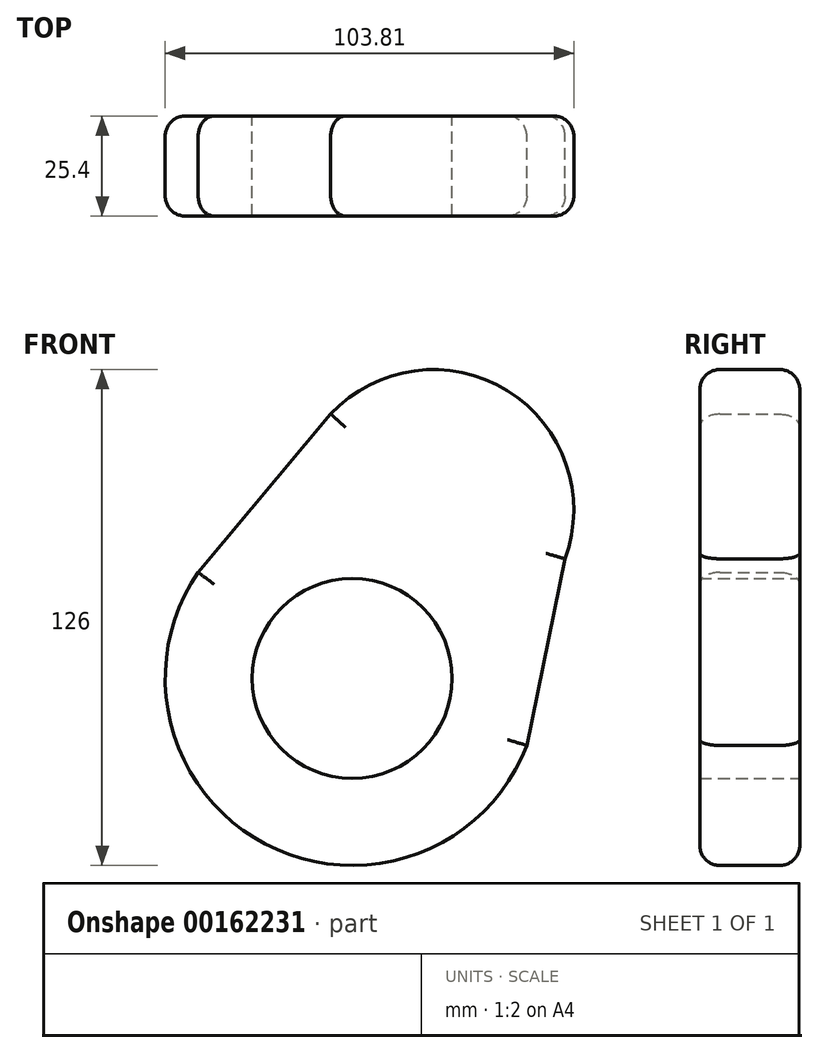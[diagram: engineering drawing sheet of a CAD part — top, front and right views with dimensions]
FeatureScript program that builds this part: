
annotation { "Feature Type Name" : "Feature", "Feature Type Description" : "" }
export const myFeature = defineFeature(function(context is Context, id is Id, definition is map)
    precondition{}
    {
        {
            var Q0;
            Q0=qCreatedBy(makeId("Front.planeOp"),FACE);
            var sketch = newSketch(context, id + "F0", { "sketchPlane" : qUnion([Q0])});
            skArc(sketch, "E0", {"start": v(-39.13, 26.95) * mm, "mid": v(-22.14, -42.04) * mm, "end": v(44.36, -17.01) * mm});
            skArc(sketch, "E1", {"start": v(54.07, 30.4) * mm, "mid": v(39.36, 73.17) * mm, "end": v(-5.46, 67.16) * mm});
            skLineSegment(sketch, "E2", {"start": v(-5.46, 67.16) * mm, "end": v(-39.13, 26.95) * mm});
            skLineSegment(sketch, "E3", {"start": v(54.07, 30.4) * mm, "end": v(44.36, -17.01) * mm});
            skSolve(sketch);
        }
        {
            var Q0;
            Q0=makeQuery(id+"F0.imprint","IMPRINT",FACE,{"disambiguationData":[TD([[makeQuery(id+"F0.imprint","IMPRINT",EDGE,{"derivedFrom":sQuery(id+"F0.wireOp",EDGE,"E0")}),1.0]])]});
            extrude(context, id + "F1", {"entities" : qUnion([Q0]), "depth" : 25.4 * mm});
        }
        {
            var Q0;
            Q0=makeQuery(id+"F1.opExtrude","CAP_EDGE",EDGE,{"disambiguationData":[OSD([sQuery(id+"F0.wireOp",EDGE,"E2")])],"isStart":false});
            var Q1;
            Q1=makeQuery(id+"F1.opExtrude","CAP_EDGE",EDGE,{"disambiguationData":[OSD([sQuery(id+"F0.wireOp",EDGE,"E1")])],"isStart":false});
            var Q2;
            Q2=makeQuery(id+"F1.opExtrude","CAP_EDGE",EDGE,{"disambiguationData":[OSD([sQuery(id+"F0.wireOp",EDGE,"E3")])],"isStart":false});
            var Q3;
            Q3=makeQuery(id+"F1.opExtrude","CAP_EDGE",EDGE,{"disambiguationData":[OSD([sQuery(id+"F0.wireOp",EDGE,"E0")])],"isStart":false});
            fillet(context, id + "F2", {"entities" : qUnion([Q0, Q1, Q2, Q3]), "radius" : 5.08 * mm, "tangentPropagation" : true, "allowEdgeOverflow" : false});
        }
        {
            var Q0;
            Q0=makeQuery(id+"F1.opExtrude","CAP_EDGE",EDGE,{"disambiguationData":[OSD([sQuery(id+"F0.wireOp",EDGE,"E2")])],"isStart":true});
            var Q1;
            Q1=makeQuery(id+"F1.opExtrude","CAP_EDGE",EDGE,{"disambiguationData":[OSD([sQuery(id+"F0.wireOp",EDGE,"E1")])],"isStart":true});
            var Q2;
            Q2=makeQuery(id+"F1.opExtrude","CAP_EDGE",EDGE,{"disambiguationData":[OSD([sQuery(id+"F0.wireOp",EDGE,"E3")])],"isStart":true});
            var Q3;
            Q3=makeQuery(id+"F1.opExtrude","CAP_EDGE",EDGE,{"disambiguationData":[OSD([sQuery(id+"F0.wireOp",EDGE,"E0")])],"isStart":true});
            fillet(context, id + "F3", {"entities" : qUnion([Q0, Q1, Q2, Q3]), "radius" : 5.08 * mm, "tangentPropagation" : true, "allowEdgeOverflow" : false});
        }
        {
            var Q0;
            Q0=qCreatedBy(makeId("Front.planeOp"),FACE);
            var sketch = newSketch(context, id + "F4", { "sketchPlane" : qUnion([Q0])});
            skCircle(sketch, "E4", {"center": v(0, 0) * mm, "radius": 25.4 * mm});
            skSolve(sketch);
        }
        {
            var Q0;
            Q0=makeQuery(id+"F4.imprint","IMPRINT",FACE,{"disambiguationData":[TD([[makeQuery(id+"F4.imprint","IMPRINT",EDGE,{"derivedFrom":sQuery(id+"F4.wireOp",EDGE,"E4")}),1.0]])]});
            var Q1;
            Q1=sQuery(id+"F4.wireOp",EDGE,"E4");
            extrude(context, id + "F5", {"entities" : qUnion([Q0]), "surfaceEntities" : qUnion([Q1]), "endBound" : BoundingType.UP_TO_NEXT, "depth" : 50.8 * mm});
        }
    });
